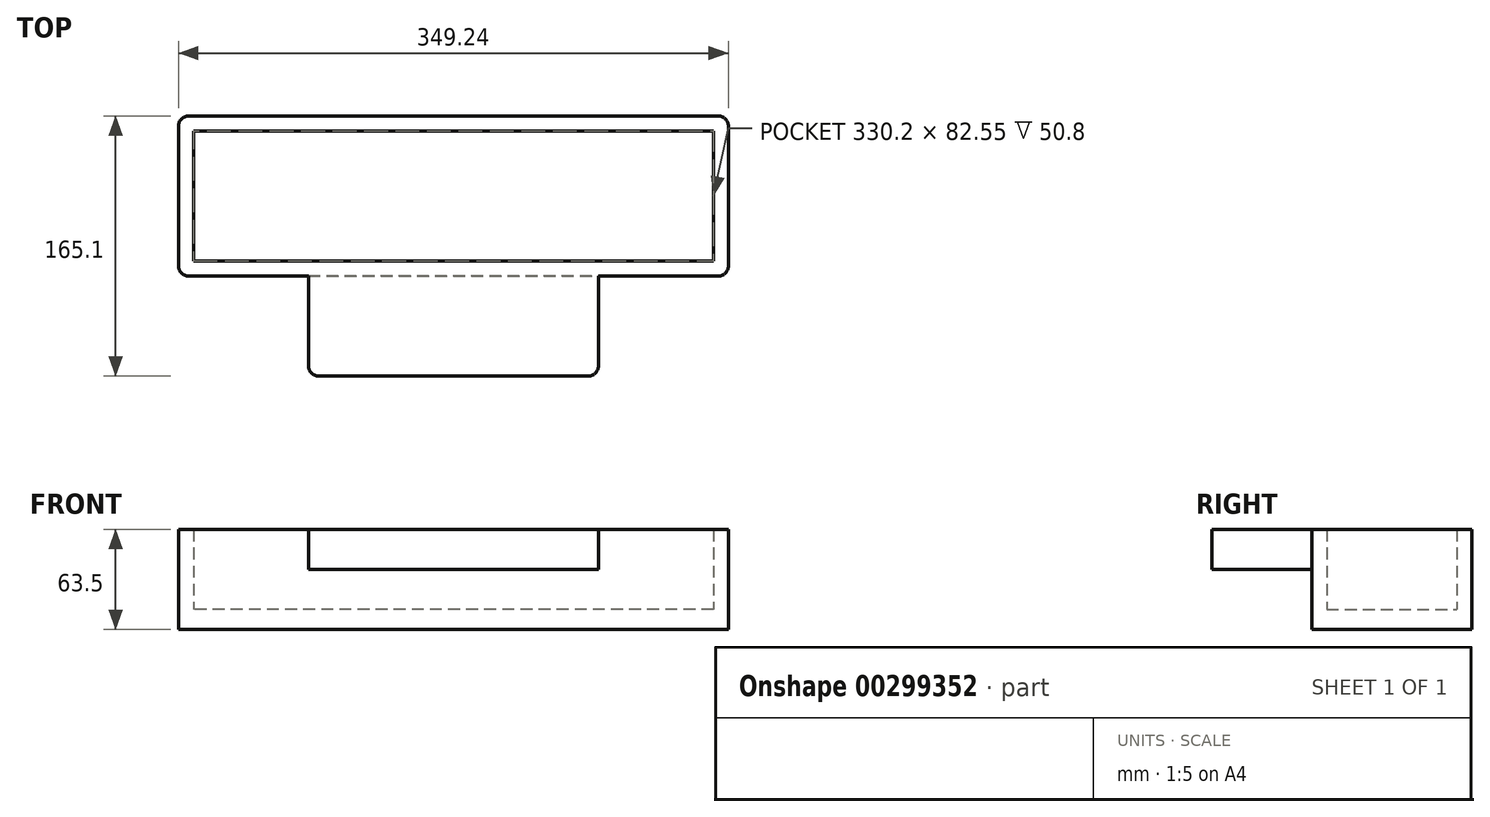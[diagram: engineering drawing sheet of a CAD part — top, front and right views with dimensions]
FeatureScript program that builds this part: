
annotation { "Feature Type Name" : "Feature", "Feature Type Description" : "" }
export const myFeature = defineFeature(function(context is Context, id is Id, definition is map)
    precondition{}
    {
        {
            var Q0;
            Q0=qCreatedBy(makeId("Top.planeOp"),FACE);
            var sketch = newSketch(context, id + "F0", { "sketchPlane" : qUnion([Q0])});
            skLineSegment(sketch, "E0.bottom", {"start": v(174.63, 50.8) * mm, "end": v(-174.63, 50.8) * mm});
            skLineSegment(sketch, "E0.top", {"start": v(174.63, -50.8) * mm, "end": v(-174.63, -50.8) * mm});
            skLineSegment(sketch, "E0.left", {"start": v(174.63, 50.8) * mm, "end": v(174.63, -50.8) * mm});
            skLineSegment(sketch, "E0.right", {"start": v(-174.63, 50.8) * mm, "end": v(-174.63, -50.8) * mm});
            skPoint(sketch, "E0.middle", {"position": v(0, 0) * mm});
            skLineSegment(sketch, "E1.bottom", {"start": v(165.1, 41.27) * mm, "end": v(-165.1, 41.28) * mm});
            skLineSegment(sketch, "E1.top", {"start": v(165.1, -41.28) * mm, "end": v(-165.1, -41.28) * mm});
            skLineSegment(sketch, "E1.left", {"start": v(165.1, 41.27) * mm, "end": v(165.1, -41.28) * mm});
            skLineSegment(sketch, "E1.right", {"start": v(-165.1, 41.28) * mm, "end": v(-165.1, -41.27) * mm});
            skSolve(sketch);
        }
        {
            var Q0;
            Q0=makeQuery(id+"F0.imprint","IMPRINT",FACE,{"disambiguationData":[TD([[makeQuery(id+"F0.imprint","IMPRINT",EDGE,{"derivedFrom":sQuery(id+"F0.wireOp",EDGE,"E0.bottom")}),1.0]])]});
            extrude(context, id + "F1", {"entities" : qUnion([Q0]), "depth" : 63.5 * mm});
        }
        {
            var Q0;
            Q0=makeQuery(id+"F1.opExtrude","SWEPT_EDGE",EDGE,{"disambiguationData":[OSD([sQuery(id+"F0.wireOp",EDGE,"E0.top"),sQuery(id+"F0.wireOp",EDGE,"E0.right")])]});
            var Q1;
            Q1=makeQuery(id+"F1.opExtrude","SWEPT_EDGE",EDGE,{"disambiguationData":[OSD([sQuery(id+"F0.wireOp",EDGE,"E0.top"),sQuery(id+"F0.wireOp",EDGE,"E0.left")])]});
            var Q2;
            Q2=makeQuery(id+"F1.opExtrude","SWEPT_EDGE",EDGE,{"disambiguationData":[OSD([sQuery(id+"F0.wireOp",EDGE,"E0.bottom"),sQuery(id+"F0.wireOp",EDGE,"E0.left")])]});
            var Q3;
            Q3=makeQuery(id+"F1.opExtrude","SWEPT_EDGE",EDGE,{"disambiguationData":[OSD([sQuery(id+"F0.wireOp",EDGE,"E0.bottom"),sQuery(id+"F0.wireOp",EDGE,"E0.right")])]});
            fillet(context, id + "F2", {"entities" : qUnion([Q0, Q1, Q2, Q3]), "radius" : 6.35 * mm, "tangentPropagation" : true, "allowEdgeOverflow" : false});
        }
        {
            var Q0;
            Q0=qCreatedBy(makeId("Top.planeOp"),FACE);
            var sketch = newSketch(context, id + "F3", { "sketchPlane" : qUnion([Q0])});
            skLineSegment(sketch, "E2.bottom", {"start": v(165.1, -41.27) * mm, "end": v(-165.1, -41.28) * mm});
            skLineSegment(sketch, "E2.top", {"start": v(165.1, 41.28) * mm, "end": v(-165.1, 41.27) * mm});
            skLineSegment(sketch, "E2.left", {"start": v(165.1, -41.27) * mm, "end": v(165.1, 41.28) * mm});
            skLineSegment(sketch, "E2.right", {"start": v(-165.1, -41.28) * mm, "end": v(-165.1, 41.27) * mm});
            skPoint(sketch, "E2.middle", {"position": v(0, 0) * mm});
            skSolve(sketch);
        }
        {
            var Q0;
            Q0 = qSketchRegion(id + "F3", true);
            extrude(context, id + "F4", {"entities" : qUnion([Q0]), "operationType" : NewBodyOperationType.ADD, "depth" : 12.7 * mm});
        }
        {
            var Q0;
            Q0=makeQuery(id+"F1.opExtrude","SWEPT_FACE",FACE,{"disambiguationData":[OSD([sQuery(id+"F0.wireOp",EDGE,"E0.top")])]});
            var sketch = newSketch(context, id + "F5", { "sketchPlane" : qUnion([Q0])});
            skLineSegment(sketch, "E3.bottom", {"start": v(-92.08, 63.5) * mm, "end": v(92.08, 63.5) * mm});
            skLineSegment(sketch, "E3.top", {"start": v(-92.08, 38.1) * mm, "end": v(92.08, 38.1) * mm});
            skLineSegment(sketch, "E3.left", {"start": v(-92.08, 63.5) * mm, "end": v(-92.08, 38.1) * mm});
            skLineSegment(sketch, "E3.right", {"start": v(92.08, 63.5) * mm, "end": v(92.08, 38.1) * mm});
            skSolve(sketch);
        }
        {
            var Q0;
            Q0=makeQuery(id+"F5.imprint","IMPRINT",FACE,{"disambiguationData":[TD([[makeQuery(id+"F5.imprint","IMPRINT",EDGE,{"derivedFrom":sQuery(id+"F5.wireOp",EDGE,"E3.bottom")}),1.0]])]});
            extrude(context, id + "F6", {"entities" : qUnion([Q0]), "operationType" : NewBodyOperationType.ADD, "depth" : 63.5 * mm});
        }
        {
            var Q0;
            Q0=makeQuery(id+"F6.opExtrude","CAP_EDGE",EDGE,{"disambiguationData":[OSD([sQuery(id+"F5.wireOp",EDGE,"E3.left")])],"isStart":false});
            var Q1;
            Q1=makeQuery(id+"F6.opExtrude","CAP_EDGE",EDGE,{"disambiguationData":[OSD([sQuery(id+"F5.wireOp",EDGE,"E3.right")])],"isStart":false});
            fillet(context, id + "F7", {"entities" : qUnion([Q0, Q1]), "radius" : 6.35 * mm, "tangentPropagation" : true, "allowEdgeOverflow" : false});
        }
    });
